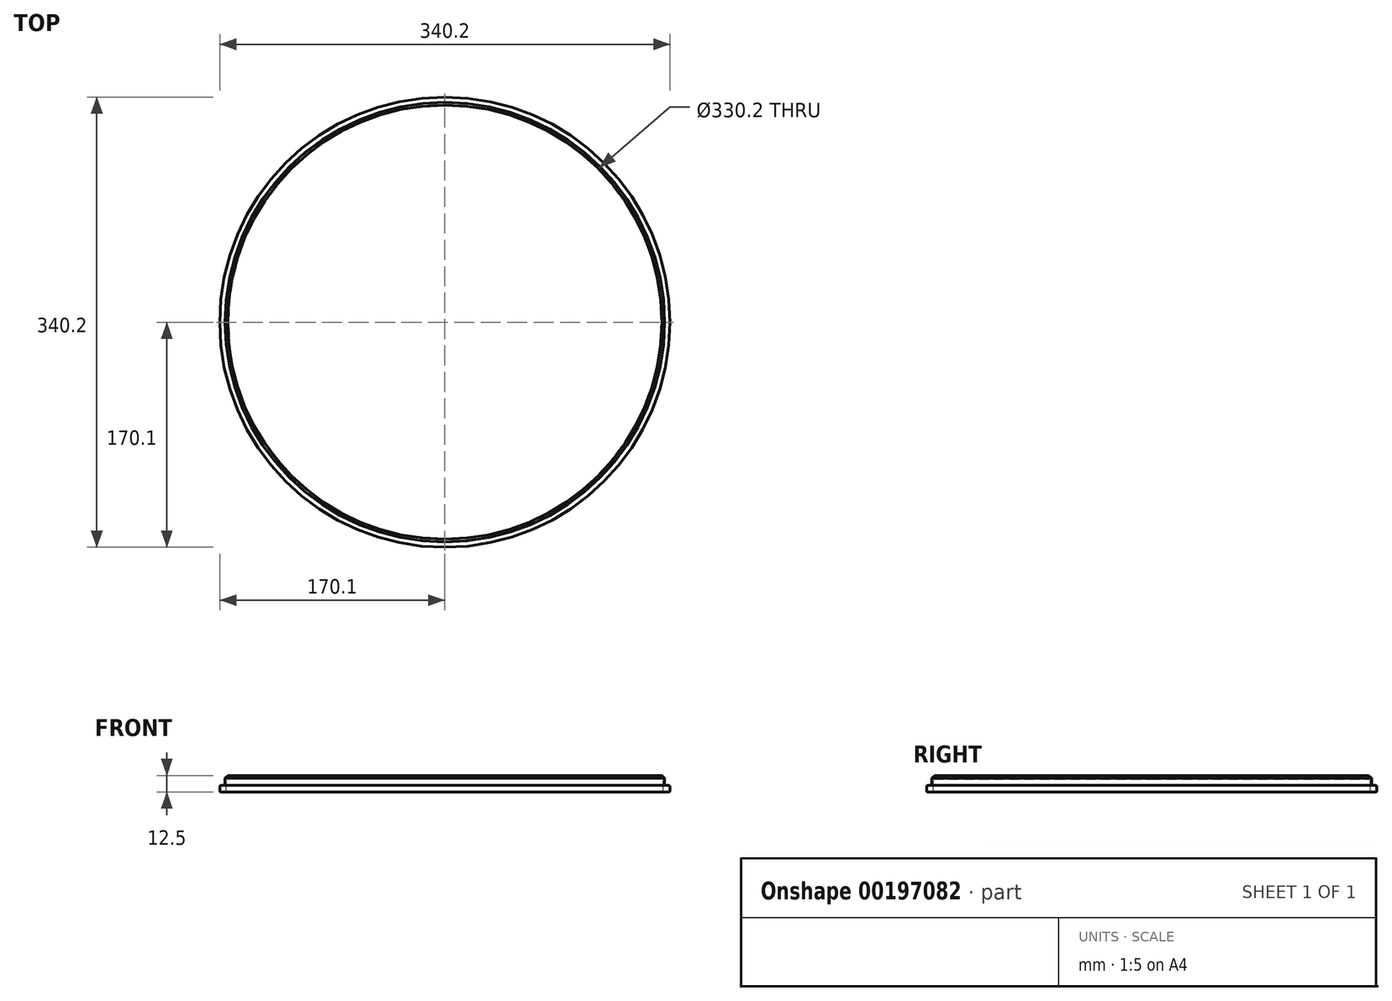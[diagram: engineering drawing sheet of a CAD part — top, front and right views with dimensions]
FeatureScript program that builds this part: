
annotation { "Feature Type Name" : "Feature", "Feature Type Description" : "" }
export const myFeature = defineFeature(function(context is Context, id is Id, definition is map)
    precondition{}
    {
        {
            var Q0;
            Q0=qCreatedBy(makeId("Front.planeOp"),FACE);
            var sketch = newSketch(context, id + "F0", { "sketchPlane" : qUnion([Q0])});
            skLineSegment(sketch, "E0", {"start": v(0, 0) * mm, "end": v(-163.6, 0) * mm});
            skLineSegment(sketch, "E1", {"start": v(-166.1, -11.5) * mm, "end": v(-169.1, -11.5) * mm});
            skLineSegment(sketch, "E2", {"start": v(-170.1, -10.5) * mm, "end": v(-170.1, -7.5) * mm});
            skLineSegment(sketch, "E3.0", {"start": v(0, 1) * mm, "end": v(-164.01, 1) * mm});
            skLineSegment(sketch, "E4", {"start": v(-165.1, -1.5) * mm, "end": v(-165.1, -10.5) * mm});
            skLineSegment(sketch, "E5", {"start": v(-165.1, -1.5) * mm, "end": v(-163.6, 0) * mm});
            skLineSegment(sketch, "E6.0", {"start": v(-166.1, -1.09) * mm, "end": v(-164.01, 1) * mm});
            skPoint(sketch, "E7.orphan", {"position": v(-165.1, 0) * mm});
            skLineSegment(sketch, "E8", {"start": v(0, 1) * mm, "end": v(0, 0) * mm});
            skPoint(sketch, "E9.visualSharp", {"position": v(-170.1, -11.5) * mm});
            skArc(sketch, "E9.filletArc", {"start": v(-170.1, -10.5) * mm, "mid": v(-169.8, -11.2) * mm, "end": v(-169.1, -11.5) * mm});
            skPoint(sketch, "E10.visualSharp", {"position": v(-170.1, -6.5) * mm});
            skArc(sketch, "E10.filletArc", {"start": v(-169.1, -6.5) * mm, "mid": v(-169.8, -6.8) * mm, "end": v(-170.1, -7.5) * mm});
            skPoint(sketch, "E11.visualSharp", {"position": v(-165.1, -11.5) * mm});
            skArc(sketch, "E11.filletArc", {"start": v(-166.1, -11.5) * mm, "mid": v(-165.4, -11.2) * mm, "end": v(-165.1, -10.5) * mm});
            skLineSegment(sketch, "E12.0", {"start": v(-166.1, -1.09) * mm, "end": v(-166.1, -6.5) * mm});
            skLineSegment(sketch, "E13", {"start": v(-169.1, -6.5) * mm, "end": v(-166.1, -6.5) * mm});
            skSolve(sketch);
        }
        {
            var Q0;
            Q0=makeQuery(id+"F0.imprint","IMPRINT",FACE,{"disambiguationData":[TD([[makeQuery(id+"F0.imprint","IMPRINT",EDGE,{"derivedFrom":sQuery(id+"F0.wireOp",EDGE,"E0")}),-1.0]])]});
            var Q1;
            Q1=sQuery(id+"F0.wireOp",EDGE,"E8");
            revolve(context, id + "F1", {"entities" : qUnion([Q0]), "axis" : qUnion([Q1]), "revolveType" : RevolveType.FULL});
        }
    });
